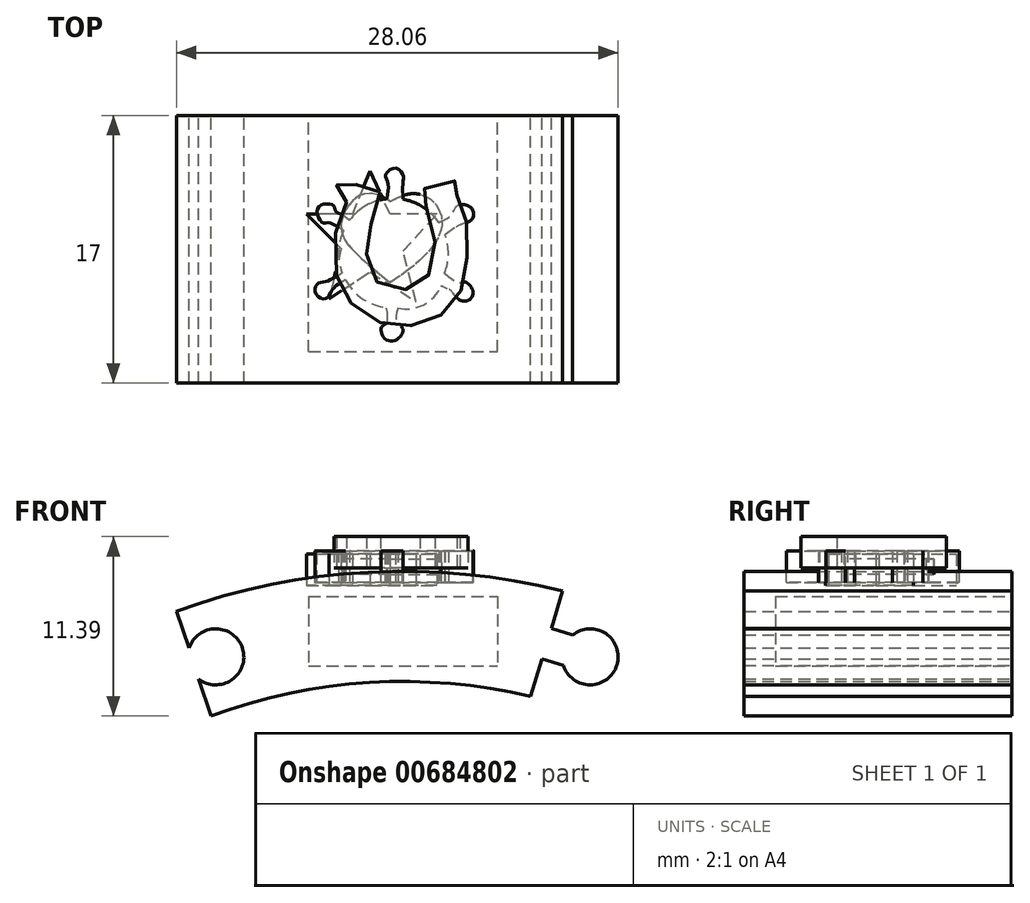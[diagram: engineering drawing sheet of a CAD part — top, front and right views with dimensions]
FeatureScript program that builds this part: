
annotation { "Feature Type Name" : "Feature", "Feature Type Description" : "" }
export const myFeature = defineFeature(function(context is Context, id is Id, definition is map)
    precondition{}
    {
        {
            var Q0;
            Q0=qCreatedBy(makeId("Front.planeOp"),FACE);
            var sketch = newSketch(context, id + "F0", { "sketchPlane" : qUnion([Q0])});
            skArc(sketch, "E0", {"start": v(8.11, 34.05) * mm, "mid": v(-2.13, 34.93) * mm, "end": v(-12.2, 32.8) * mm});
            skLineSegment(sketch, "E1", {"start": v(0, 35) * mm, "end": v(0, 38.2) * mm, "construction": true});
            skLineSegment(sketch, "E2.bottom", {"start": v(-6, 40.4) * mm, "end": v(6, 40.4) * mm});
            skLineSegment(sketch, "E2.top", {"start": v(-6, 36) * mm, "end": v(6, 36) * mm});
            skLineSegment(sketch, "E2.left", {"start": v(-6, 40.4) * mm, "end": v(-6, 36) * mm});
            skLineSegment(sketch, "E2.right", {"start": v(6, 40.4) * mm, "end": v(6, 36) * mm});
            skPoint(sketch, "E2.middle", {"position": v(0, 38.2) * mm});
            skArc(sketch, "E3.0", {"start": v(10.14, 40.76) * mm, "mid": v(-2.22, 41.94) * mm, "end": v(-14.4, 39.46) * mm});
            skLineSegment(sketch, "E4", {"start": v(0, 0) * mm, "end": v(0, 85.1) * mm, "construction": true});
            skLineSegment(sketch, "E5", {"start": v(8.11, 34.05) * mm, "end": v(8.84, 36.44) * mm});
            skLineSegment(sketch, "E6", {"start": v(9.13, 37.4) * mm, "end": v(10.18, 37.08) * mm, "construction": true});
            skArc(sketch, "E7", {"start": v(10.19, 36.04) * mm, "mid": v(13.6, 36.05) * mm, "end": v(10.77, 37.95) * mm});
            skLineSegment(sketch, "E8.0", {"start": v(8.84, 36.44) * mm, "end": v(10.19, 36.04) * mm});
            skLineSegment(sketch, "E9.MirrorCS", {"start": v(9.42, 38.36) * mm, "end": v(10.77, 37.95) * mm});
            skArc(sketch, "E10.MirrorC", {"start": v(10.77, 37.95) * mm, "mid": v(13.6, 36.05) * mm, "end": v(10.19, 36.04) * mm});
            skLineSegment(sketch, "E11.trimOffspring", {"start": v(9.42, 38.36) * mm, "end": v(10.14, 40.76) * mm});
            skLineSegment(sketch, "E12.MirrorCS", {"start": v(-9.13, 37.4) * mm, "end": v(-10.18, 37.08) * mm, "construction": true});
            skArc(sketch, "E13.MirrorCS", {"start": v(-10.19, 36.04) * mm, "mid": v(-11.36, 34.87) * mm, "end": v(-12.98, 35.16) * mm});
            skArc(sketch, "E14.MirrorCS", {"start": v(-10.19, 36.04) * mm, "mid": v(-11.34, 38.26) * mm, "end": v(-13.58, 37.12) * mm});
            skArc(sketch, "E15.trimOffspring", {"start": v(-13.58, 37.12) * mm, "mid": v(-12.4, 38.27) * mm, "end": v(-10.77, 37.95) * mm});
            skArc(sketch, "E16.trimOffspring", {"start": v(-12.98, 35.16) * mm, "mid": v(-11.36, 34.87) * mm, "end": v(-10.19, 36.04) * mm});
            skLineSegment(sketch, "E17", {"start": v(-13.58, 37.12) * mm, "end": v(-14.4, 39.46) * mm});
            skLineSegment(sketch, "E18", {"start": v(-12.98, 35.16) * mm, "end": v(-12.2, 32.8) * mm});
            skSolve(sketch);
        }
        {
            var Q0;
            Q0=makeQuery(id+"F0.imprint","IMPRINT",FACE,{"disambiguationData":[TD([[makeQuery(id+"F0.imprint","IMPRINT",EDGE,{"derivedFrom":sQuery(id+"F0.wireOp",EDGE,"E0")}),-1.0]])]});
            var Q1;
            Q1=makeQuery(id+"F0.imprint","IMPRINT",FACE,{"disambiguationData":[TD([[makeQuery(id+"F0.imprint","IMPRINT",EDGE,{"derivedFrom":sQuery(id+"F0.wireOp",EDGE,"E2.bottom")}),-1.0]])]});
            extrude(context, id + "F1", {"entities" : qUnion([Q0, Q1]), "depth" : 17 * mm, "offsetDistance" : 25 * mm});
        }
        {
            var Q0;
            Q0=makeQuery(id+"F0.imprint","IMPRINT",FACE,{"disambiguationData":[TD([[makeQuery(id+"F0.imprint","IMPRINT",EDGE,{"derivedFrom":sQuery(id+"F0.wireOp",EDGE,"E2.bottom")}),-1.0]])]});
            extrude(context, id + "F2", {"entities" : qUnion([Q0]), "operationType" : NewBodyOperationType.REMOVE, "depth" : 15 * mm, "offsetDistance" : 25 * mm});
        }
        {
            var Q0;
            Q0=qCreatedBy(makeId("Top.planeOp"),FACE);
            var sketch = newSketch(context, id + "F3", { "sketchPlane" : qUnion([Q0])});
            skFitSpline(sketch, "E19", {"points": [v(-1, -5.45) * mm, v(-2.24, -4.95) * mm, v(-3.1, -5.2) * mm, v(-3.81, -5.98) * mm, v(-4.1, -6.83) * mm, v(-3.85, -7.93) * mm, v(-1, -10.6) * mm], "startDerivative": vector(-9.04, 5.97) * mm, "endDerivative": vector(12.81, -10.36) * mm});
            skFitSpline(sketch, "E20.MirrorCS", {"points": [v(-1, -5.45) * mm, v(0.15, -5) * mm, v(1.23, -5.12) * mm, v(2, -5.8) * mm, v(2.3, -6.79) * mm, v(1.96, -7.92) * mm, v(-1, -10.6) * mm], "startDerivative": vector(8.16, 3.92) * mm, "endDerivative": vector(-18.12, -11.26) * mm});
            skSolve(sketch);
        }
        {
            var Q0;
            Q0 = qSketchRegion(id + "F3", true);
            extrude(context, id + "F4", {"entities" : qUnion([Q0]), "depth" : 1 * mm, "offsetDistance" : 25 * mm});
        }
        {
            var Q0;
            Q0=makeQuery(id+"F4.opExtrude","SWEPT_BODY",BODY,{"disambiguationData":[OSD([sQuery(id+"F3.wireOp",EDGE,"E19"),sQuery(id+"F3.wireOp",EDGE,"E20.MirrorCS")])]});
            transform(context, id + "F5", {"entities" : qUnion([Q0]), "transformType" : TransformType.TRANSLATION_3D, "dx" : 0.18 * mm, "dy" : 0 * mm, "dz" : 41.8 * mm, "makeCopy" : false});
        }
        {
            var Q0;
            Q0=qCreatedBy(makeId("Top.planeOp"),FACE);
            var sketch = newSketch(context, id + "F6", { "sketchPlane" : qUnion([Q0])});
            skLineSegment(sketch, "E21", {"start": v(-2.1, -3.53) * mm, "end": v(-3.21, -6.26) * mm});
            skLineSegment(sketch, "E22", {"start": v(-3.21, -6.26) * mm, "end": v(-6.11, -6.26) * mm});
            skLineSegment(sketch, "E23", {"start": v(-6.11, -6.26) * mm, "end": v(-3.92, -8.45) * mm});
            skLineSegment(sketch, "E24", {"start": v(-3.92, -8.45) * mm, "end": v(-4.7, -11.66) * mm});
            skLineSegment(sketch, "E25", {"start": v(-4.7, -11.66) * mm, "end": v(-2.1, -9.94) * mm});
            skLineSegment(sketch, "E26", {"start": v(-2.1, -9.94) * mm, "end": v(0.83, -11.82) * mm});
            skLineSegment(sketch, "E27", {"start": v(0.83, -11.82) * mm, "end": v(0, -8.62) * mm});
            skLineSegment(sketch, "E28", {"start": v(0, -8.62) * mm, "end": v(2.15, -6.26) * mm});
            skLineSegment(sketch, "E29", {"start": v(2.15, -6.26) * mm, "end": v(-0.82, -6.26) * mm});
            skLineSegment(sketch, "E30", {"start": v(-0.82, -6.26) * mm, "end": v(-2.1, -3.53) * mm});
            skSolve(sketch);
        }
        {
            var Q0;
            Q0 = qSketchRegion(id + "F6", true);
            extrude(context, id + "F7", {"entities" : qUnion([Q0]), "depth" : 2 * mm, "offsetDistance" : 25 * mm});
        }
        {
            var Q0;
            Q0=makeQuery(id+"F7.opExtrude","SWEPT_BODY",BODY,{"disambiguationData":[OSD([sQuery(id+"F6.wireOp",EDGE,"E21"),sQuery(id+"F6.wireOp",EDGE,"E22"),sQuery(id+"F6.wireOp",EDGE,"E23"),sQuery(id+"F6.wireOp",EDGE,"E24"),sQuery(id+"F6.wireOp",EDGE,"E25"),sQuery(id+"F6.wireOp",EDGE,"E26"),sQuery(id+"F6.wireOp",EDGE,"E27"),sQuery(id+"F6.wireOp",EDGE,"E28"),sQuery(id+"F6.wireOp",EDGE,"E29"),sQuery(id+"F6.wireOp",EDGE,"E30")])]});
            transform(context, id + "F8", {"entities" : qUnion([Q0]), "transformType" : TransformType.TRANSLATION_3D, "dx" : 0 * mm, "dy" : 0 * mm, "dz" : 41.1 * mm, "makeCopy" : false});
        }
        {
            var Q0;
            Q0=qCreatedBy(makeId("Top.planeOp"),FACE);
            var sketch = newSketch(context, id + "F9", { "sketchPlane" : qUnion([Q0])});
            skArc(sketch, "E31", {"start": v(-3.79, -7.3) * mm, "mid": v(-4.1, -8.64) * mm, "end": v(-3.87, -9.99) * mm});
            skFitSpline(sketch, "E32", {"points": [v(-3.79, -7.3) * mm, v(-4.7, -6.81) * mm, v(-5.06, -6.81) * mm, v(-5.4, -6.41) * mm, v(-5.36, -5.83) * mm, v(-4.85, -5.6) * mm, v(-4.4, -5.72) * mm, v(-4.3, -6.05) * mm, v(-3.82, -6.34) * mm, v(-3.39, -6.64) * mm], "startDerivative": vector(-6.5, 4.5) * mm, "endDerivative": vector(3.6, -2.9) * mm});
            skFitSpline(sketch, "E33", {"points": [v(2.28, -6.78) * mm, v(3.12, -6.27) * mm, v(3.45, -5.72) * mm, v(4.33, -5.86) * mm, v(4.4, -6.56) * mm, v(3.78, -6.89) * mm, v(3.27, -7.14) * mm, v(2.68, -7.58) * mm], "startDerivative": vector(6.16, 2.57) * mm, "endDerivative": vector(-4.23, -3.35) * mm});
            skFitSpline(sketch, "E34", {"points": [v(2.65, -10) * mm, v(3.52, -10.61) * mm, v(3.92, -10.58) * mm, v(4.44, -11.13) * mm, v(4.14, -11.75) * mm, v(3.49, -11.64) * mm, v(3.12, -11.2) * mm, v(2.43, -10.83) * mm], "startDerivative": vector(5.3, -4.86) * mm, "endDerivative": vector(-5.04, 1.78) * mm});
            skFitSpline(sketch, "E35", {"points": [v(-0.32, -12.23) * mm, v(-0.39, -13.1) * mm, v(0, -13.57) * mm, v(-0.35, -14.2) * mm, v(-1.12, -14.2) * mm, v(-1.37, -13.46) * mm, v(-1.05, -13.17) * mm, v(-1.04, -12.21) * mm], "startDerivative": vector(-1.72, -6.2) * mm, "endDerivative": vector(-1.17, 7.03) * mm});
            skFitSpline(sketch, "E36", {"points": [v(-3.66, -10.44) * mm, v(-4.47, -11.05) * mm, v(-4.94, -11.64) * mm, v(-5.56, -11.27) * mm, v(-5.42, -10.69) * mm, v(-4.87, -10.54) * mm, v(-3.87, -9.99) * mm], "startDerivative": vector(-4.81, -2.71) * mm, "endDerivative": vector(5.2, 3.52) * mm});
            skArc(sketch, "E37.trimOffspring", {"start": v(-3.66, -10.44) * mm, "mid": v(-2.56, -11.64) * mm, "end": v(-1.04, -12.21) * mm});
            skArc(sketch, "E38.trimOffspring", {"start": v(2.65, -10) * mm, "mid": v(2.88, -8.8) * mm, "end": v(2.68, -7.58) * mm});
            skArc(sketch, "E39.trimOffspring", {"start": v(2.28, -6.78) * mm, "mid": v(1.29, -5.82) * mm, "end": v(0, -5.31) * mm});
            skPoint(sketch, "E40.3.internal.snap0", {"position": v(-0.52, -5.26) * mm});
            skFitSpline(sketch, "E40", {"points": [v(-1.02, -5.28) * mm, v(-0.96, -4.26) * mm, v(-1.1, -3.78) * mm, v(-0.52, -3.34) * mm, v(0, -3.74) * mm, v(0, -4.22) * mm, v(0, -5.31) * mm], "startDerivative": vector(1.05, 5.78) * mm, "endDerivative": vector(0.22, -5.96) * mm});
            skArc(sketch, "E41.trimOffspring", {"start": v(-1.02, -5.28) * mm, "mid": v(-2.34, -5.72) * mm, "end": v(-3.39, -6.64) * mm});
            skArc(sketch, "E42", {"start": v(-0.32, -12.23) * mm, "mid": v(1.3, -12.02) * mm, "end": v(2.43, -10.83) * mm});
            skSolve(sketch);
        }
        {
            var Q0;
            Q0 = qSketchRegion(id + "F9", true);
            extrude(context, id + "F10", {"entities" : qUnion([Q0]), "depth" : 2 * mm, "offsetDistance" : 25 * mm});
        }
        {
            var Q0;
            Q0=makeQuery(id+"F10.opExtrude","SWEPT_BODY",BODY,{"disambiguationData":[OSD([sQuery(id+"F9.wireOp",EDGE,"E31"),sQuery(id+"F9.wireOp",EDGE,"E32"),sQuery(id+"F9.wireOp",EDGE,"E33"),sQuery(id+"F9.wireOp",EDGE,"E34"),sQuery(id+"F9.wireOp",EDGE,"E35"),sQuery(id+"F9.wireOp",EDGE,"E36"),sQuery(id+"F9.wireOp",EDGE,"E37.trimOffspring"),sQuery(id+"F9.wireOp",EDGE,"E38.trimOffspring"),sQuery(id+"F9.wireOp",EDGE,"E39.trimOffspring"),sQuery(id+"F9.wireOp",EDGE,"E40"),sQuery(id+"F9.wireOp",EDGE,"E41.trimOffspring"),sQuery(id+"F9.wireOp",EDGE,"E42")])]});
            transform(context, id + "F11", {"entities" : qUnion([Q0]), "transformType" : TransformType.TRANSLATION_3D, "dx" : 1.08E-16 * mm, "dy" : 0 * mm, "dz" : 50.4 * mm, "makeCopy" : false});
        }
        {
            var Q0;
            Q0=qCreatedBy(makeId("Top.planeOp"),FACE);
            var sketch = newSketch(context, id + "F12", { "sketchPlane" : qUnion([Q0])});
            skFitSpline(sketch, "E43", {"points": [v(-1.47, -4.86) * mm, v(-2.09, -7.04) * mm, v(-2.3, -8.86) * mm, v(-1.67, -10.55) * mm, v(0, -11.08) * mm, v(1.42, -10.42) * mm, v(2.04, -8.53) * mm, v(1.46, -5.77) * mm, v(1.09, -4.9) * mm, v(2.28, -4.32) * mm, v(3.6, -4.24) * mm, v(3.44, -4.98) * mm, v(3.93, -6.3) * mm, v(4.1, -8.78) * mm, v(3.73, -11.04) * mm, v(2.45, -12.65) * mm, v(0.51, -13.35) * mm, v(-1.43, -13.15) * mm, v(-3.4, -11.79) * mm, v(-4.27, -9.93) * mm, v(-4.02, -6.43) * mm, v(-3.61, -5.23) * mm, v(-4.23, -4.49) * mm, v(-3.61, -4.2) * mm, v(-2.7, -4.49) * mm, v(-1.47, -4.86) * mm]});
            skSolve(sketch);
        }
        {
            var Q0;
            Q0 = qSketchRegion(id + "F12", true);
            extrude(context, id + "F13", {"entities" : qUnion([Q0]), "depth" : 2 * mm, "offsetDistance" : 25 * mm});
        }
        {
            var Q0;
            Q0=makeQuery(id+"F10.opExtrude","SWEPT_BODY",BODY,{"disambiguationData":[OSD([sQuery(id+"F9.wireOp",EDGE,"E31"),sQuery(id+"F9.wireOp",EDGE,"E32"),sQuery(id+"F9.wireOp",EDGE,"E33"),sQuery(id+"F9.wireOp",EDGE,"E34"),sQuery(id+"F9.wireOp",EDGE,"E35"),sQuery(id+"F9.wireOp",EDGE,"E36"),sQuery(id+"F9.wireOp",EDGE,"E37.trimOffspring"),sQuery(id+"F9.wireOp",EDGE,"E38.trimOffspring"),sQuery(id+"F9.wireOp",EDGE,"E39.trimOffspring"),sQuery(id+"F9.wireOp",EDGE,"E40"),sQuery(id+"F9.wireOp",EDGE,"E41.trimOffspring"),sQuery(id+"F9.wireOp",EDGE,"E42")])]});
            transform(context, id + "F14", {"entities" : qUnion([Q0]), "transformType" : TransformType.TRANSLATION_3D, "dx" : 0 * mm, "dy" : 0 * mm, "dz" : -9.1 * mm, "makeCopy" : false});
        }
        {
            var Q0;
            Q0=makeQuery(id+"F13.opExtrude","SWEPT_BODY",BODY,{"disambiguationData":[OSD([sQuery(id+"F12.wireOp",EDGE,"E43")])]});
            transform(context, id + "F15", {"entities" : qUnion([Q0]), "transformType" : TransformType.TRANSLATION_3D, "dx" : 0 * mm, "dy" : 0 * mm, "dz" : 42.2 * mm, "makeCopy" : false});
        }
    });
